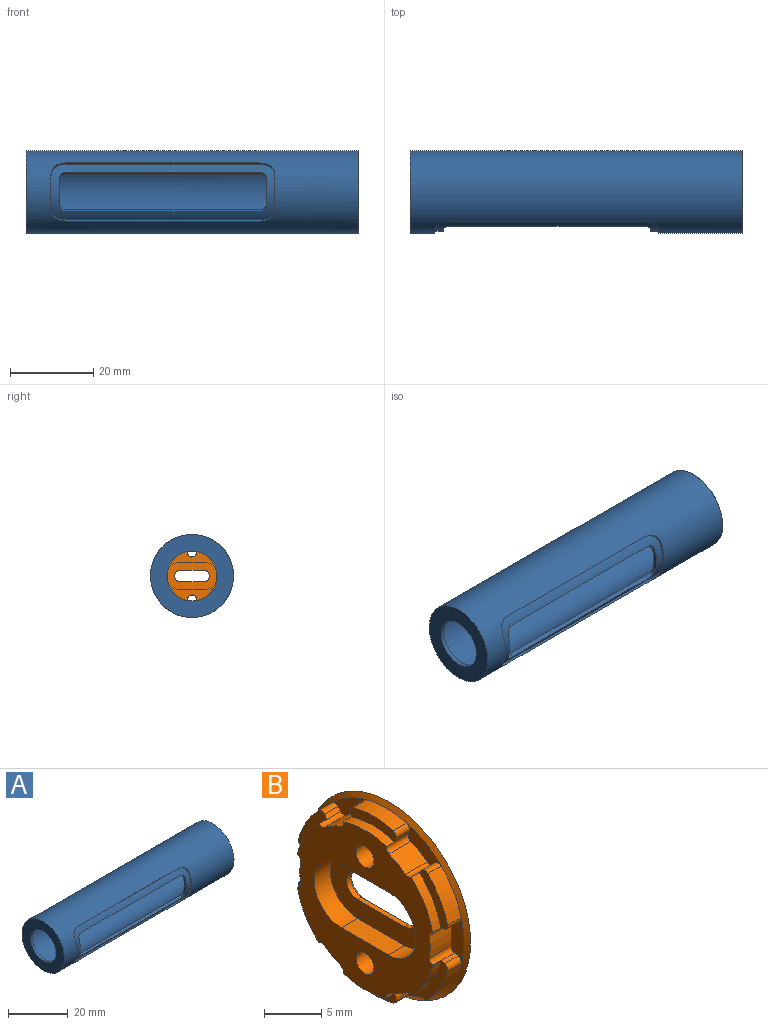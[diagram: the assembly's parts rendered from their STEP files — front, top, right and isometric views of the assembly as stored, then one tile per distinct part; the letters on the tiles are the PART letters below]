
ASSEMBLY  parts=2 mates=1
PART A: 109 faces, bbox 80.1x20.7x20.1 mm
  f0: cylinder r=8.55mm len=0.42mm, axis (1,0,0), area 0mm2, adj f20,f60,f65
  f1: cylinder r=8.55mm len=3.03mm, axis (1,0,0), area 0.2mm2, adj f21,f30,f59,f73,f74
  f2: cylinder r=8.55mm len=3.5mm, axis (1,0,0), area 0.2mm2, adj f29,f36,f89,f91
  f3: cylinder r=8.55mm len=3.03mm, axis (1,0,0), area 0.2mm2, adj f35,f42,f85,f86
  f4: cylinder r=8.55mm len=3.03mm, axis (1,0,0), area 0.2mm2, adj f41,f48,f81,f82
  f5: cylinder r=8.55mm len=3.5mm, axis (1,0,0), area 0.2mm2, adj f47,f54,f77,f78
  f6: cylinder r=8.55mm len=3.03mm, axis (1,0,0), area 0.2mm2, adj f53,f60,f63,f64
  f7: cylinder r=8.55mm len=3.03mm, axis (1,0,0), area 0.2mm2, adj f30,f59,f67,f72
  f8: cylinder r=8.55mm len=3.5mm, axis (1,0,0), area 0.2mm2, adj f29,f36,f70,f88
  f9: cylinder r=8.55mm len=3.03mm, axis (1,0,0), area 0.2mm2, adj f35,f42,f69,f84
  f10: cylinder r=8.55mm len=3.03mm, axis (1,0,0), area 0.2mm2, adj f41,f48,f68,f80
  f11: cylinder r=8.55mm len=3.5mm, axis (1,0,0), area 0.2mm2, adj f47,f54,f68,f76
  f12: cylinder r=8.55mm len=73.78mm, axis (1,0,0), area 3493.6mm2, adj f19,f24,f66,f68,f71,f92,f93,f94
  f13: cylinder r=8.55mm len=17.1mm, axis (1,0,0), area 1.9mm2, adj f14,f53,f59,f60,f61,f62,f66,f68
  f14: cylinder r=8.55mm len=17.1mm, axis (1,0,0), area 3.4mm2, adj f13,f15,f66,f68
  f15: cylinder r=8.55mm len=17.1mm, axis (1,0,0), area 3.4mm2, adj f14,f16,f66,f68
  f16: cylinder r=8.55mm len=17.1mm, axis (1,0,0), area 3.4mm2, adj f15,f17,f66,f68
  f17: cylinder r=8.55mm len=17.1mm, axis (1,0,0), area 3.4mm2, adj f16,f18,f66,f68
  f18: cylinder r=8.55mm len=17.1mm, axis (1,0,0), area 3.4mm2, adj f17,f19,f66,f68
  f19: cylinder r=8.55mm len=17.1mm, axis (1,0,0), area 3.4mm2, adj f12,f18,f66,f68
  f20: cone r=10mm half-angle=55.4deg, axis (1,0,0), area 59.3mm2, adj f0,f25,f26,f27,f28,f29,f30,f32
  f21: cone r=10mm half-angle=55.4deg, axis (1,0,0), area 0mm2, adj f1,f59,f74
  f22: plane 20x20mm, normal (-1,0,0), area 201.1mm2, adj f23,f25
  f23: cylinder r=6mm len=12mm, axis (1,0,0), area 37.7mm2, adj f22,f24
  f24: plane 17.1x17.1mm, normal (1,0,0), area 116.6mm2, adj f12,f23
  f25: cylinder r=10mm len=80mm, axis (1,0,0), area 4222mm2, adj f20,f22,f101,f102,f103,f104,f105,f106
  f26: cylinder r=0.5mm len=1.66mm, axis (1,0,0), area 1.2mm2, adj f20,f27,f29,f31
  f27: cylinder r=9.5mm len=4.26mm, axis (1,0,0), area 8.2mm2, adj f20,f26,f28,f31
  f28: cylinder r=0.5mm len=1.66mm, axis (1,0,0), area 1.2mm2, adj f20,f27,f30,f31
  f29: plane 1.3x0.43mm, normal (0,-0.2,0.98), area 0.3mm2, adj f2,f8,f20,f26,f31,f66,f70,f88
  f30: plane 1.3x0.33mm, normal (0,0.75,-0.67), area 0.3mm2, adj f1,f7,f20,f28,f31,f66,f67,f72
  f31: plane 5.13x3.51mm, normal (1,0,0), area 4.9mm2, adj f26,f27,f28,f29,f30,f66
  f32: cylinder r=0.5mm len=1.66mm, axis (1,0,0), area 1.2mm2, adj f20,f33,f35,f37
  f33: cylinder r=9.5mm len=4.26mm, axis (1,0,0), area 8.2mm2, adj f20,f32,f34,f37
  f34: cylinder r=0.5mm len=1.66mm, axis (1,0,0), area 1.2mm2, adj f20,f33,f36,f37
  f35: plane 1.3x0.33mm, normal (0,0.75,0.67), area 0.3mm2, adj f3,f9,f20,f32,f37,f66,f69,f84
  f36: plane 1.3x0.43mm, normal (0,-0.2,-0.98), area 0.3mm2, adj f2,f8,f20,f34,f37,f66,f70,f88
  f37: plane 5.12x3.35mm, normal (1,0,0), area 4.1mm2, adj f32,f33,f34,f35,f36,f66
  f38: cylinder r=0.5mm len=1.66mm, axis (1,0,0), area 1.2mm2, adj f20,f39,f41,f43
  f39: cylinder r=9.5mm len=4.92mm, axis (1,0,0), area 8.2mm2, adj f20,f38,f40,f43
  f40: cylinder r=0.5mm len=1.66mm, axis (1,0,0), area 1.2mm2, adj f20,f39,f42,f43
  f41: plane 1.3x0.41mm, normal (0,0.95,-0.31), area 0.3mm2, adj f4,f10,f20,f38,f43,f68,f80,f81
  f42: plane 1.3x0.41mm, normal (0,-0.95,-0.31), area 0.3mm2, adj f3,f9,f20,f40,f43,f66,f69,f84
  f43: plane 5.71x1.12mm, normal (1,0,0), area 3.3mm2, adj f38,f39,f40,f41,f42,f66,f68
  f44: cylinder r=0.5mm len=1.66mm, axis (1,0,0), area 1.2mm2, adj f20,f45,f47,f49
  f45: cylinder r=9.5mm len=4.26mm, axis (1,0,0), area 8.2mm2, adj f20,f44,f46,f49
  f46: cylinder r=0.5mm len=1.66mm, axis (1,0,0), area 1.2mm2, adj f20,f45,f48,f49
  f47: plane 1.3x0.43mm, normal (0,0.2,-0.98), area 0.3mm2, adj f5,f11,f20,f44,f49,f68,f76,f77
  f48: plane 1.3x0.33mm, normal (0,-0.75,0.67), area 0.3mm2, adj f4,f10,f20,f46,f49,f68,f80,f81
  f49: plane 5.12x3.35mm, normal (1,0,0), area 4mm2, adj f44,f45,f46,f47,f48,f68
  f50: cylinder r=0.5mm len=1.66mm, axis (1,0,0), area 1.2mm2, adj f20,f51,f53,f55
  f51: cylinder r=9.5mm len=4.26mm, axis (1,0,0), area 8.2mm2, adj f20,f50,f52,f55
  f52: cylinder r=0.5mm len=1.66mm, axis (1,0,0), area 1.2mm2, adj f20,f51,f54,f55
  f53: plane 1.3x0.33mm, normal (0,-0.75,-0.67), area 0.3mm2, adj f6,f13,f20,f50,f55,f62,f63,f64
  f54: plane 1.3x0.43mm, normal (0,0.2,0.98), area 0.3mm2, adj f5,f11,f20,f52,f55,f68,f76,f77
  f55: plane 5.14x3.51mm, normal (1,0,0), area 4.8mm2, adj f50,f51,f52,f53,f54,f68
  f56: cylinder r=0.5mm len=1.66mm, axis (1,0,0), area 1.2mm2, adj f20,f57,f59,f61
  f57: cylinder r=9.5mm len=4.92mm, axis (1,0,0), area 8.2mm2, adj f20,f56,f58,f61
  f58: cylinder r=0.5mm len=1.66mm, axis (1,0,0), area 1.2mm2, adj f20,f57,f60,f61
  f59: plane 1.3x0.41mm, normal (0,-0.95,0.31), area 0.3mm2, adj f1,f7,f13,f20,f21,f56,f61,f66
  f60: plane 1.3x0.41mm, normal (0,0.95,0.31), area 0.3mm2, adj f0,f6,f13,f20,f58,f61,f62,f63
  f61: plane 5.66x1.38mm, normal (1,0,0), area 5.3mm2, adj f13,f56,f57,f58,f59,f60
  f62: bspline ~7.73x4.68mm, area 1.6mm2, adj f13,f53,f60,f63
  f63: bspline ~7.73x4.68mm, area 1.6mm2, adj f6,f53,f60,f62
  f64: bspline ~7.73x4.68mm, area 1.6mm2, adj f6,f53,f60,f65
  f65: bspline ~7.73x4.68mm, area 1.5mm2, adj f0,f20,f53,f60,f64
  f66: bspline ~20.62x17.86mm, area 188.8mm2, adj f12,f13,f14,f15,f16,f17,f18,f19
  f67: bspline ~7.73x4.68mm, area 1.6mm2, adj f7,f30,f59,f66
  f68: bspline ~20.62x17.86mm, area 176.8mm2, adj f10,f11,f12,f13,f14,f15,f16,f17
  f69: bspline ~7.73x4.68mm, area 1.6mm2, adj f9,f35,f42,f66
  f70: bspline ~8.93x2.95mm, area 1.6mm2, adj f8,f29,f36,f66
  f71: plane 0.44x0.38mm, normal (0,-1,0), area 0.1mm2, adj f12,f66,f68
  f72: bspline ~7.73x4.68mm, area 1.6mm2, adj f7,f30,f59,f73
  f73: bspline ~7.73x4.68mm, area 1.6mm2, adj f1,f30,f59,f72
  f74: bspline ~7.73x4.68mm, area 1.5mm2, adj f1,f21,f30,f59,f75
  f75: bspline ~7.73x4.68mm, area 0.2mm2, adj f20,f30,f59,f74
  f76: bspline ~8.93x2.95mm, area 1.6mm2, adj f11,f47,f54,f77
  f77: bspline ~8.93x2.95mm, area 1.6mm2, adj f5,f47,f54,f76
  f78: bspline ~8.93x2.95mm, area 1.6mm2, adj f5,f47,f54,f79
  f79: bspline ~8.93x2.95mm, area 1.3mm2, adj f20,f47,f54,f78
  f80: bspline ~7.73x4.68mm, area 1.6mm2, adj f10,f41,f48,f81
  f81: bspline ~7.73x4.68mm, area 1.6mm2, adj f4,f41,f48,f80
  f82: bspline ~7.73x4.68mm, area 1.6mm2, adj f4,f41,f48,f83
  f83: bspline ~7.73x4.68mm, area 1mm2, adj f20,f41,f48,f82
  f84: bspline ~7.73x4.68mm, area 1.6mm2, adj f9,f35,f42,f85
  f85: bspline ~7.73x4.68mm, area 1.6mm2, adj f3,f35,f42,f84
  f86: bspline ~7.73x4.68mm, area 1.6mm2, adj f3,f35,f42,f87
  f87: bspline ~7.73x4.68mm, area 0.7mm2, adj f20,f35,f42,f86
  f88: bspline ~8.93x2.95mm, area 1.6mm2, adj f8,f29,f36,f89
  f89: bspline ~8.93x2.95mm, area 1.6mm2, adj f2,f29,f36,f88
  f90: bspline ~8.93x2.95mm, area 0.4mm2, adj f20,f29,f36,f91
  f91: bspline ~8.93x2.95mm, area 1.6mm2, adj f2,f29,f36,f90
  f92: plane 46x0.82mm, normal (0,-0.5,-0.87), area 43.7mm2, adj f12,f98,f99,f100
  f93: plane 5.82x1.3mm, normal (-1,0,0), area 5.1mm2, adj f12,f96,f98,f100
  f94: plane 46x0.82mm, normal (0,-0.5,0.87), area 43.7mm2, adj f12,f96,f97,f100
  f95: plane 5.82x1.3mm, normal (1,0,0), area 5.1mm2, adj f12,f97,f99,f100
  f96: bspline ~2.66x2.61mm, area 3.1mm2, adj f12,f93,f94,f100
  f97: bspline ~2.66x2.61mm, area 3.1mm2, adj f12,f94,f95,f100
  f98: bspline ~2.66x2.61mm, area 3.1mm2, adj f12,f92,f93,f100
  f99: bspline ~2.66x2.61mm, area 3.1mm2, adj f12,f92,f95,f100
  f100: cylinder r=9.5mm len=54mm, axis (-1,0,0), area 295.5mm2, adj f92,f93,f94,f95,f96,f97,f98,f99
  f101: plane 46x0.36mm, normal (0,-0.7,-0.71), area 23mm2, adj f25,f100,f107,f108
  f102: plane 7.12x1.05mm, normal (-1,0,0), area 3.4mm2, adj f25,f100,f105,f107
  f103: plane 46x0.36mm, normal (0,-0.7,0.71), area 23mm2, adj f25,f100,f105,f106
  f104: plane 7.12x1.05mm, normal (1,0,0), area 3.4mm2, adj f25,f100,f106,f108
  f105: bspline ~4x3.92mm, area 3.3mm2, adj f25,f100,f102,f103
  f106: bspline ~4x3.92mm, area 3.3mm2, adj f25,f100,f103,f104
  f107: bspline ~4x3.92mm, area 3.3mm2, adj f25,f100,f101,f102
  f108: bspline ~4x3.92mm, area 3.3mm2, adj f25,f100,f101,f104
PART B: 86 faces, bbox 3x20x20 mm
  f0: plane 17x16.64mm, normal (-1,0,0), area 135.9mm2, adj f17,f18,f19,f20,f21,f24,f25,f26
  f1: cylinder r=1.35mm len=2.7mm, axis (1,0,0), area 2.1mm2, adj f2,f4,f78,f81
  f2: plane 5.8x0.5mm, normal (0,0,1), area 2.9mm2, adj f1,f3,f80,f81
  f3: cylinder r=1.35mm len=2.7mm, axis (1,0,0), area 2.1mm2, adj f2,f4,f79,f81
  f4: plane 5.8x0.5mm, normal (0,0,-1), area 2.9mm2, adj f1,f3,f77,f81
  f5: plane 20x20mm, normal (1,0,0), area 256.8mm2, adj f22,f74,f76,f77,f78,f79,f80
  f6: cylinder r=9.5mm len=4.92mm, axis (-1,0,0), area 8.3mm2, adj f12,f22,f63,f66
  f7: cylinder r=9.5mm len=4.26mm, axis (-1,0,0), area 8.3mm2, adj f13,f22,f55,f61
  f8: cylinder r=9.5mm len=4.26mm, axis (-1,0,0), area 8.3mm2, adj f14,f22,f47,f53
  f9: cylinder r=9.5mm len=4.92mm, axis (-1,0,0), area 8.3mm2, adj f15,f22,f39,f45
  f10: cylinder r=9.5mm len=4.26mm, axis (-1,0,0), area 8.3mm2, adj f16,f22,f31,f37
  f11: cylinder r=9.5mm len=4.26mm, axis (-1,0,0), area 8.3mm2, adj f22,f23,f29,f67
  f12: plane 5.66x1.42mm, normal (-1,0,0), area 5.6mm2, adj f6,f17,f62,f63,f66,f68
  f13: plane 5.12x3.53mm, normal (-1,0,0), area 5.6mm2, adj f7,f18,f54,f55,f60,f61
  f14: plane 5.12x3.53mm, normal (-1,0,0), area 5.6mm2, adj f8,f19,f46,f47,f52,f53
  f15: plane 5.66x1.42mm, normal (-1,0,0), area 5.6mm2, adj f9,f20,f38,f39,f44,f45
  f16: plane 5.12x3.53mm, normal (-1,0,0), area 5.6mm2, adj f10,f21,f30,f31,f36,f37
  f17: cylinder r=8.5mm len=5.31mm, axis (-1,0,0), area 5.4mm2, adj f0,f12,f59,f70
  f18: cylinder r=8.5mm len=4.59mm, axis (-1,0,0), area 5.4mm2, adj f0,f13,f51,f58
  f19: cylinder r=8.5mm len=4.59mm, axis (-1,0,0), area 5.4mm2, adj f0,f14,f43,f50
  f20: cylinder r=8.5mm len=5.31mm, axis (-1,0,0), area 5.4mm2, adj f0,f15,f35,f42
  f21: cylinder r=8.5mm len=4.59mm, axis (-1,0,0), area 5.4mm2, adj f0,f16,f27,f34
  f22: cone r=10mm half-angle=56.3deg, axis (1,0,0), area 36.8mm2, adj f5,f6,f7,f8,f9,f10,f11,f32
  f23: plane 5.12x3.53mm, normal (-1,0,0), area 5.6mm2, adj f11,f24,f28,f29,f67,f69
  f24: cylinder r=8.5mm len=4.59mm, axis (-1,0,0), area 5.4mm2, adj f0,f23,f26,f72
  f25: cylinder r=8.01mm len=2.67mm, axis (1,0,0), area 6.3mm2, adj f0,f26,f27,f32
  f26: cylinder r=0.5mm len=2.67mm, axis (1,0,0), area 2mm2, adj f0,f24,f25,f28,f32
  f27: cylinder r=0.5mm len=2.67mm, axis (1,0,0), area 2mm2, adj f0,f21,f25,f30,f32
  f28: plane 1.67x0.48mm, normal (0,0.2,-0.98), area 0.8mm2, adj f23,f26,f29,f32
  f29: cylinder r=0.5mm len=1.67mm, axis (1,0,0), area 1.4mm2, adj f11,f23,f28,f32
  f30: plane 1.67x0.48mm, normal (0,0.2,0.98), area 0.8mm2, adj f16,f27,f31,f32
  f31: cylinder r=0.5mm len=1.67mm, axis (1,0,0), area 1.4mm2, adj f10,f16,f30,f32
  f32: plane 4.92x1.58mm, normal (-1,0,0), area 5.4mm2, adj f22,f25,f26,f27,f28,f29,f30,f31
  f33: cylinder r=8.01mm len=2.67mm, axis (1,0,0), area 6.3mm2, adj f0,f34,f35,f40
  f34: cylinder r=0.5mm len=2.67mm, axis (1,0,0), area 2mm2, adj f0,f21,f33,f36,f40
  f35: cylinder r=0.5mm len=2.67mm, axis (1,0,0), area 2mm2, adj f0,f20,f33,f38,f40
  f36: plane 1.67x0.36mm, normal (0,-0.75,-0.67), area 0.8mm2, adj f16,f34,f37,f40
  f37: cylinder r=0.5mm len=1.67mm, axis (1,0,0), area 1.4mm2, adj f10,f16,f36,f40
  f38: plane 1.67x0.46mm, normal (0,0.95,0.31), area 0.8mm2, adj f15,f35,f39,f40
  f39: cylinder r=0.5mm len=1.67mm, axis (1,0,0), area 1.4mm2, adj f9,f15,f38,f40
  f40: plane 4.26x3.01mm, normal (-1,0,0), area 5.4mm2, adj f22,f33,f34,f35,f36,f37,f38,f39
  f41: cylinder r=8.01mm len=2.67mm, axis (1,0,0), area 6.3mm2, adj f0,f42,f43,f48
  f42: cylinder r=0.5mm len=2.67mm, axis (1,0,0), area 2mm2, adj f0,f20,f41,f44,f48
  f43: cylinder r=0.5mm len=2.67mm, axis (1,0,0), area 2mm2, adj f0,f19,f41,f46,f48
  f44: plane 1.67x0.46mm, normal (0,-0.95,0.31), area 0.8mm2, adj f15,f42,f45,f48
  f45: cylinder r=0.5mm len=1.67mm, axis (1,0,0), area 1.4mm2, adj f9,f15,f44,f48
  f46: plane 1.67x0.36mm, normal (0,0.75,-0.67), area 0.8mm2, adj f14,f43,f47,f48
  f47: cylinder r=0.5mm len=1.67mm, axis (1,0,0), area 1.4mm2, adj f8,f14,f46,f48
  f48: plane 4.26x3.01mm, normal (-1,0,0), area 5.4mm2, adj f22,f41,f42,f43,f44,f45,f46,f47
  f49: cylinder r=8.01mm len=2.67mm, axis (1,0,0), area 6.3mm2, adj f0,f50,f51,f56
  f50: cylinder r=0.5mm len=2.67mm, axis (1,0,0), area 2mm2, adj f0,f19,f49,f52,f56
  f51: cylinder r=0.5mm len=2.67mm, axis (1,0,0), area 2mm2, adj f0,f18,f49,f54,f56
  f52: plane 1.67x0.48mm, normal (0,-0.2,0.98), area 0.8mm2, adj f14,f50,f53,f56
  f53: cylinder r=0.5mm len=1.67mm, axis (1,0,0), area 1.4mm2, adj f8,f14,f52,f56
  f54: plane 1.67x0.48mm, normal (0,-0.2,-0.98), area 0.8mm2, adj f13,f51,f55,f56
  f55: cylinder r=0.5mm len=1.67mm, axis (1,0,0), area 1.4mm2, adj f7,f13,f54,f56
  f56: plane 4.92x1.58mm, normal (-1,0,0), area 5.4mm2, adj f22,f49,f50,f51,f52,f53,f54,f55
  f57: cylinder r=8.01mm len=2.67mm, axis (1,0,0), area 6.3mm2, adj f0,f58,f59,f64
  f58: cylinder r=0.5mm len=2.67mm, axis (1,0,0), area 2mm2, adj f0,f18,f57,f60,f64
  f59: cylinder r=0.5mm len=2.67mm, axis (1,0,0), area 2mm2, adj f0,f17,f57,f62,f64
  f60: plane 1.67x0.36mm, normal (0,0.75,0.67), area 0.8mm2, adj f13,f58,f61,f64
  f61: cylinder r=0.5mm len=1.67mm, axis (1,0,0), area 1.4mm2, adj f7,f13,f60,f64
  f62: plane 1.67x0.46mm, normal (0,-0.95,-0.31), area 0.8mm2, adj f12,f59,f63,f64
  f63: cylinder r=0.5mm len=1.67mm, axis (1,0,0), area 1.4mm2, adj f6,f12,f62,f64
  f64: plane 4.26x3.01mm, normal (-1,0,0), area 5.4mm2, adj f22,f57,f58,f59,f60,f61,f62,f63
  f65: plane 4.26x3.01mm, normal (-1,0,0), area 5.4mm2, adj f22,f66,f67,f68,f69,f70,f71,f72
  f66: cylinder r=0.5mm len=1.67mm, axis (1,0,0), area 1.4mm2, adj f6,f12,f65,f68
  f67: cylinder r=0.5mm len=1.67mm, axis (1,0,0), area 1.4mm2, adj f11,f23,f65,f69
  f68: plane 1.67x0.46mm, normal (0,0.95,-0.31), area 0.8mm2, adj f12,f65,f66,f70
  f69: plane 1.67x0.36mm, normal (0,-0.75,0.67), area 0.8mm2, adj f23,f65,f67,f72
  f70: cylinder r=0.5mm len=2.67mm, axis (1,0,0), area 2mm2, adj f0,f17,f65,f68,f71
  f71: cylinder r=8.01mm len=2.67mm, axis (1,0,0), area 6.3mm2, adj f0,f65,f70,f72
  f72: cylinder r=0.5mm len=2.67mm, axis (1,0,0), area 2mm2, adj f0,f24,f65,f69,f71
  f73: cylinder r=1.1mm len=2.2mm, axis (1,0,0), area 14.5mm2, adj f0,f74
  f74: cone r=1.1mm half-angle=45deg, axis (1,0,0), area 12.4mm2, adj f5,f73
  f75: cylinder r=1.1mm len=2.2mm, axis (1,0,0), area 14.5mm2, adj f0,f76
  f76: cone r=1.1mm half-angle=45deg, axis (1,0,0), area 12.4mm2, adj f5,f75
  f77: plane 5.8x0.5mm, normal (0.71,0,-0.71), area 4.1mm2, adj f4,f5,f78,f79
  f78: cone r=1.85mm half-angle=45deg, axis (1,0,0), area 3.6mm2, adj f1,f5,f77,f80
  f79: cone r=1.35mm half-angle=45deg, axis (1,0,0), area 3.6mm2, adj f3,f5,f77,f80
  f80: plane 5.8x0.5mm, normal (0.71,0,0.71), area 4.1mm2, adj f2,f5,f78,f79
  f81: plane 12.5x6.7mm, normal (-1,0,0), area 52.7mm2, adj f1,f2,f3,f4,f82,f83,f84,f85
  f82: cylinder r=3.35mm len=6.7mm, axis (-1,0,0), area 21mm2, adj f0,f81,f83,f85
  f83: plane 5.8x2mm, normal (0,0,1), area 11.6mm2, adj f0,f81,f82,f84
  f84: cylinder r=3.35mm len=6.7mm, axis (-1,0,0), area 21mm2, adj f0,f81,f83,f85
  f85: plane 5.8x2mm, normal (0,0,-1), area 11.6mm2, adj f0,f81,f82,f84
PLACE A at identity
PLACE B rot(axis=(1,0,0),0deg) t=(0,0,0)mm
MATE fastened B.f6 <-> A.f0  axis (1,0,0) through (0,0,0)mm
